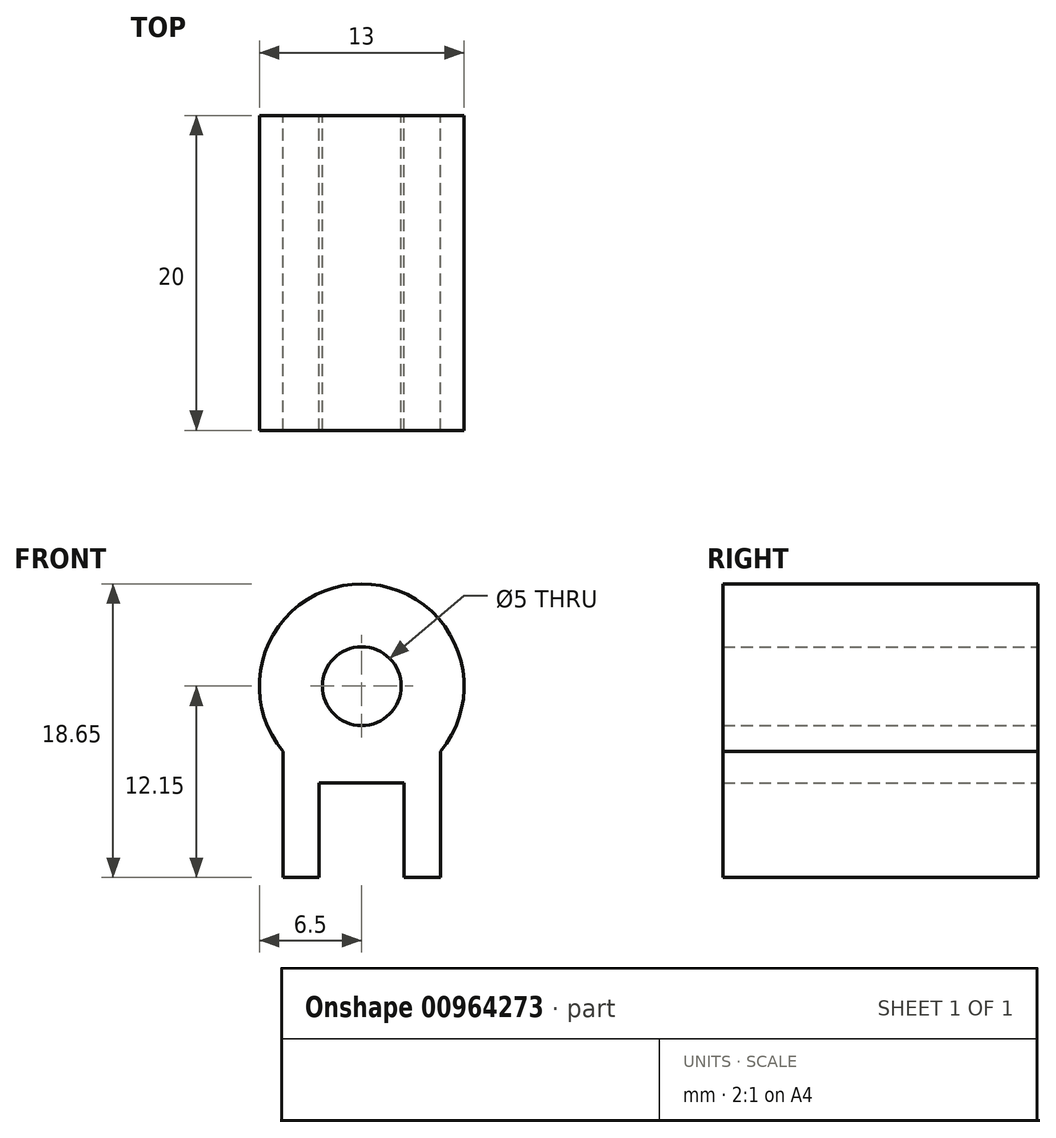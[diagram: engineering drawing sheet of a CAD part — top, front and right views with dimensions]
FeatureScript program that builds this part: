
annotation { "Feature Type Name" : "Feature", "Feature Type Description" : "" }
export const myFeature = defineFeature(function(context is Context, id is Id, definition is map)
    precondition{}
    {
        {
            var Q0;
            Q0=qCreatedBy(makeId("Front.planeOp"),FACE);
            var sketch = newSketch(context, id + "F0", { "sketchPlane" : qUnion([Q0])});
            skCircle(sketch, "E0", {"center": v(0, 0) * mm, "radius": 2.5 * mm});
            skArc(sketch, "E1", {"start": v(5, -4.15) * mm, "mid": v(0, 6.5) * mm, "end": v(-5, -4.15) * mm});
            skLineSegment(sketch, "E2", {"start": v(5, -4.15) * mm, "end": v(5, -12.15) * mm});
            skLineSegment(sketch, "E3", {"start": v(5, -12.15) * mm, "end": v(-5, -12.15) * mm});
            skLineSegment(sketch, "E4", {"start": v(-5, -12.15) * mm, "end": v(-5, -4.15) * mm});
            skLineSegment(sketch, "E5", {"start": v(-5, -4.15) * mm, "end": v(5, -4.15) * mm, "construction": true});
            skLineSegment(sketch, "E6", {"start": v(0, -12.15) * mm, "end": v(0, -4.15) * mm, "construction": true});
            skLineSegment(sketch, "E7", {"start": v(-2.7, -12.15) * mm, "end": v(-2.7, -6.15) * mm});
            skLineSegment(sketch, "E8", {"start": v(-2.7, -6.15) * mm, "end": v(2.7, -6.15) * mm});
            skLineSegment(sketch, "E9", {"start": v(2.7, -6.15) * mm, "end": v(2.7, -12.15) * mm});
            skPoint(sketch, "E10", {"position": v(0, -6.15) * mm});
            skSolve(sketch);
        }
        {
            var Q0;
            Q0=makeQuery(id+"F0.imprint","IMPRINT",FACE,{"disambiguationData":[TD([[makeQuery(id+"F0.imprint","IMPRINT",EDGE,{"derivedFrom":sQuery(id+"F0.wireOp",EDGE,"E0")}),-1.0]])]});
            extrude(context, id + "F1", {"entities" : qUnion([Q0]), "depth" : 20 * mm, "offsetDistance" : 25 * mm});
        }
    });
